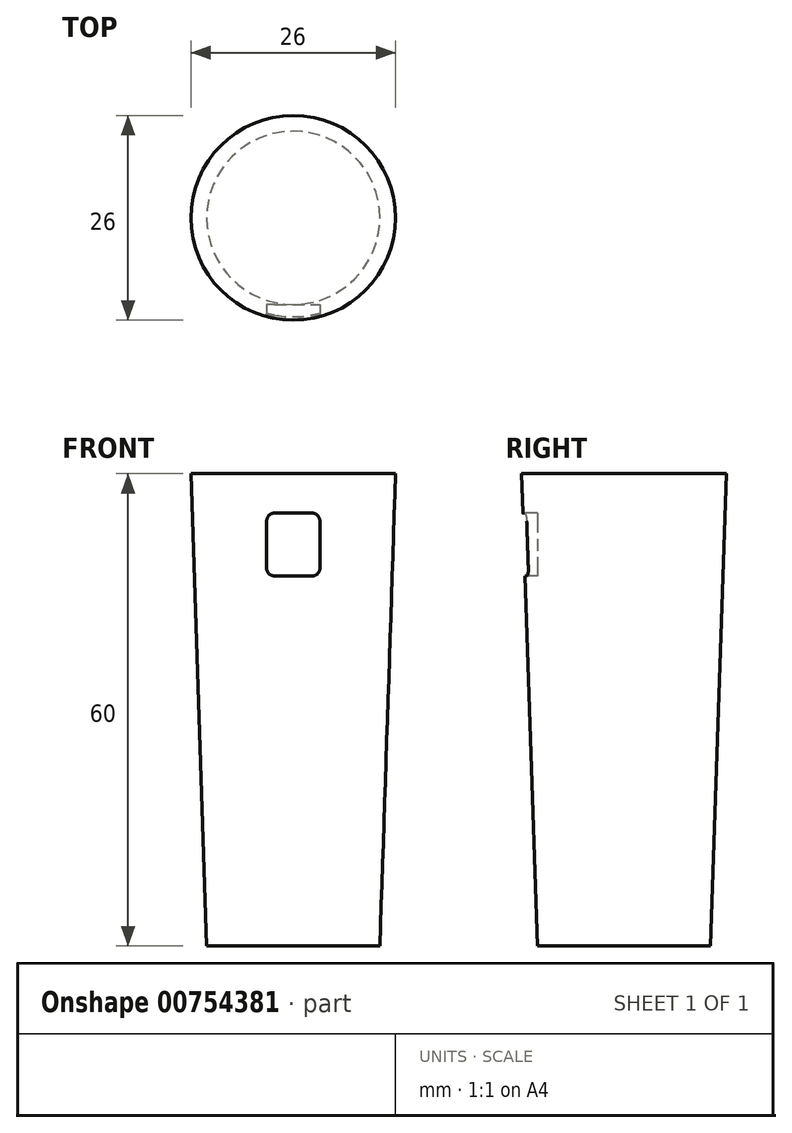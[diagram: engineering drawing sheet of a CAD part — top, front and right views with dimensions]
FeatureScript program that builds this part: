
annotation { "Feature Type Name" : "Feature", "Feature Type Description" : "" }
export const myFeature = defineFeature(function(context is Context, id is Id, definition is map)
    precondition{}
    {
        {
            var Q0;
            Q0=qCreatedBy(makeId("Top.planeOp"),FACE);
            var sketch = newSketch(context, id + "F0", { "sketchPlane" : qUnion([Q0])});
            skCircle(sketch, "E0", {"center": v(0, 0) * mm, "radius": 13 * mm});
            skSolve(sketch);
        }
        {
            var Q0;
            Q0=qCreatedBy(makeId("Top.planeOp"),FACE);
            cPlane(context, id + "F1", {"entities" : qUnion([Q0]), "cplaneType" : CPlaneType.OFFSET, "offset" : 60 * mm, "oppositeDirection" : true, "width" : 150 * mm, "height" : 150 * mm});
        }
        {
            var Q0;
            Q0=qCreatedBy(id+"F1.planeOp",FACE);
            var sketch = newSketch(context, id + "F2", { "sketchPlane" : qUnion([Q0])});
            skCircle(sketch, "E1", {"center": v(0, 0) * mm, "radius": 11 * mm});
            skSolve(sketch);
        }
        {
            var Q0;
            Q0=makeQuery(id+"F0.imprint","IMPRINT",FACE,{"disambiguationData":[TD([[makeQuery(id+"F0.imprint","IMPRINT",EDGE,{"derivedFrom":sQuery(id+"F0.wireOp",EDGE,"E0")}),1.0]])]});
            var Q1;
            Q1=makeQuery(id+"F2.imprint","IMPRINT",FACE,{"disambiguationData":[TD([[makeQuery(id+"F2.imprint","IMPRINT",EDGE,{"derivedFrom":sQuery(id+"F2.wireOp",EDGE,"E1")}),1.0]])]});
            loft(context, id + "F3", {"sheetProfilesArray" : [{ "sheetProfileEntities" : qUnion([Q0]) }, { "sheetProfileEntities" : qUnion([Q1]) }]});
        }
        {
            var Q0;
            Q0=qCreatedBy(makeId("Front.planeOp"),FACE);
            cPlane(context, id + "F4", {"entities" : qUnion([Q0]), "cplaneType" : CPlaneType.OFFSET, "offset" : 25 * mm, "width" : 150 * mm, "height" : 150 * mm});
        }
        {
            var Q0;
            Q0=qCreatedBy(id+"F4.planeOp",FACE);
            var sketch = newSketch(context, id + "F5", { "sketchPlane" : qUnion([Q0])});
            skLineSegment(sketch, "E2", {"start": v(0, 0) * mm, "end": v(0, -5) * mm});
            skLineSegment(sketch, "E3", {"start": v(0, -5) * mm, "end": v(0, -9) * mm});
            skLineSegment(sketch, "E4.bottom", {"start": v(-2.38, -5) * mm, "end": v(2.38, -5) * mm});
            skLineSegment(sketch, "E4.top", {"start": v(-2.38, -13) * mm, "end": v(2.38, -13) * mm});
            skLineSegment(sketch, "E4.left", {"start": v(-3.38, -6) * mm, "end": v(-3.38, -12) * mm});
            skLineSegment(sketch, "E4.right", {"start": v(3.38, -6) * mm, "end": v(3.38, -12) * mm});
            skPoint(sketch, "E4.middle", {"position": v(0, -9) * mm});
            skPoint(sketch, "E5.visualSharp", {"position": v(-3.38, -13) * mm});
            skArc(sketch, "E5.filletArc", {"start": v(-3.38, -12) * mm, "mid": v(-3.1, -12.7) * mm, "end": v(-2.38, -13) * mm});
            skPoint(sketch, "E6.visualSharp", {"position": v(3.38, -13) * mm});
            skArc(sketch, "E6.filletArc", {"start": v(2.38, -13) * mm, "mid": v(3.1, -12.7) * mm, "end": v(3.38, -12) * mm});
            skPoint(sketch, "E7.visualSharp", {"position": v(-3.38, -5) * mm});
            skArc(sketch, "E7.filletArc", {"start": v(-2.38, -5) * mm, "mid": v(-3.1, -5.3) * mm, "end": v(-3.38, -6) * mm});
            skPoint(sketch, "E8.visualSharp", {"position": v(3.38, -5) * mm});
            skArc(sketch, "E8.filletArc", {"start": v(3.38, -6) * mm, "mid": v(3.1, -5.3) * mm, "end": v(2.38, -5) * mm});
            skSolve(sketch);
        }
        {
            var Q0;
            Q0 = qSketchRegion(id + "F5", true);
            extrude(context, id + "F6", {"entities" : qUnion([Q0]), "operationType" : NewBodyOperationType.REMOVE, "oppositeDirection" : true, "depth" : 14 * mm, "offsetDistance" : 25 * mm});
        }
    });
